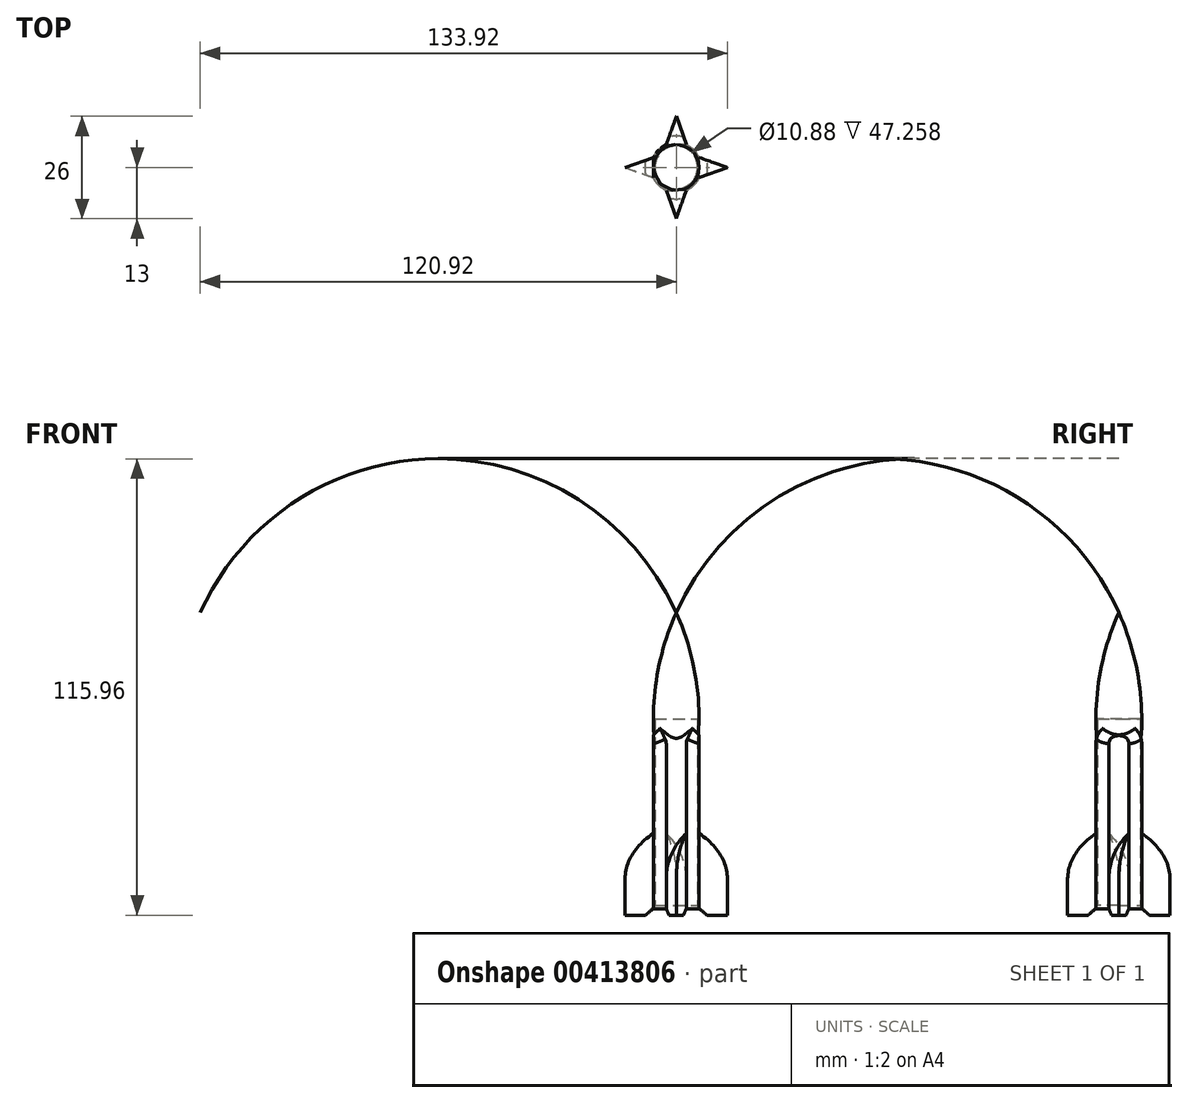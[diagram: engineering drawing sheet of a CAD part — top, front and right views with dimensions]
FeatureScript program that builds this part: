
annotation { "Feature Type Name" : "Feature", "Feature Type Description" : "" }
export const myFeature = defineFeature(function(context is Context, id is Id, definition is map)
    precondition{}
    {
        {
            var Q0;
            Q0=qCreatedBy(makeId("Top.planeOp"),FACE);
            var sketch = newSketch(context, id + "F0", { "sketchPlane" : qUnion([Q0])});
            skCircle(sketch, "E0", {"center": v(0, 0) * mm, "radius": 6.35 * mm});
            skLineSegment(sketch, "E1", {"start": v(5.82, 2.54) * mm, "end": v(13, 0) * mm});
            skLineSegment(sketch, "E2", {"start": v(13, 0) * mm, "end": v(5.82, -2.54) * mm});
            skLineSegment(sketch, "E3", {"start": v(-2.54, 5.82) * mm, "end": v(0, 13) * mm});
            skLineSegment(sketch, "E4", {"start": v(0, 13) * mm, "end": v(2.54, 5.82) * mm});
            skLineSegment(sketch, "E5", {"start": v(-5.82, 2.54) * mm, "end": v(-13, 0) * mm});
            skLineSegment(sketch, "E6", {"start": v(-13, 0) * mm, "end": v(-5.82, -2.54) * mm});
            skLineSegment(sketch, "E7", {"start": v(-2.54, -5.82) * mm, "end": v(0, -13) * mm});
            skLineSegment(sketch, "E8", {"start": v(0, -13) * mm, "end": v(2.54, -5.82) * mm});
            skCircle(sketch, "E9", {"center": v(0, 0) * mm, "radius": 5.44 * mm});
            skLineSegment(sketch, "E10", {"start": v(-5.82, -2.54) * mm, "end": v(-5.82, 2.54) * mm});
            skLineSegment(sketch, "E11", {"start": v(-2.54, -5.82) * mm, "end": v(2.54, -5.82) * mm});
            skLineSegment(sketch, "E12", {"start": v(5.82, -2.54) * mm, "end": v(5.82, 2.54) * mm});
            skLineSegment(sketch, "E13", {"start": v(2.54, 5.82) * mm, "end": v(-2.54, 5.82) * mm});
            skSolve(sketch);
        }
        {
            var Q0;
            {var subQ0=sQuery(id+"F0.wireOp",EDGE,"E0");var subQ5=makeQuery(id+"F0.imprint","INTERSECT",VERTEX,{"derivedFrom":[subQ0,sQuery(id+"F0.wireOp",EDGE,"E1")]});Q0=makeQuery(id+"F0.imprint","IMPRINT",FACE,{"disambiguationData":[TD([[makeQuery(id+"F0.imprint","IMPRINT",EDGE,{"disambiguationData":[TD([[subQ5,-1.0]])],"derivedFrom":subQ0}),1.0]])]});}
            var Q1;
            Q1=sQuery(id+"F0.wireOp",EDGE,"E0");
            extrude(context, id + "F1", {"entities" : qUnion([Q0]), "surfaceEntities" : qUnion([Q1]), "depth" : 50.8 * mm});
        }
        {
            var Q0;
            Q0 = qSketchRegion(id + "F0", true);
            extrude(context, id + "F2", {"entities" : qUnion([Q0]), "operationType" : NewBodyOperationType.ADD, "depth" : 25.4 * mm});
        }
        {
            var Q0;
            Q0=qCreatedBy(makeId("Front.planeOp"),FACE);
            var sketch = newSketch(context, id + "F3", { "sketchPlane" : qUnion([Q0])});
            skLineSegment(sketch, "E14", {"start": v(0, 49.8) * mm, "end": v(0, 76.85) * mm});
            skLineSegment(sketch, "E15", {"start": v(0, 49.8) * mm, "end": v(5.83, 49.8) * mm});
            skArc(sketch, "E16", {"start": v(5.83, 49.8) * mm, "mid": v(4.34, 63.63) * mm, "end": v(0, 76.85) * mm});
            skSolve(sketch);
        }
        {
            var Q0;
            Q0=makeQuery(id+"F2.opExtrude","CAP_EDGE",EDGE,{"disambiguationData":[OSD([sQuery(id+"F0.wireOp",EDGE,"E2")])],"isStart":false});
            var Q1;
            Q1=makeQuery(id+"F2.opExtrude","CAP_EDGE",EDGE,{"disambiguationData":[OSD([sQuery(id+"F0.wireOp",EDGE,"E4")])],"isStart":false});
            var Q2;
            Q2=makeQuery(id+"F2.opExtrude","CAP_EDGE",EDGE,{"disambiguationData":[OSD([sQuery(id+"F0.wireOp",EDGE,"E5")])],"isStart":false});
            var Q3;
            Q3=makeQuery(id+"F2.opExtrude","CAP_EDGE",EDGE,{"disambiguationData":[OSD([sQuery(id+"F0.wireOp",EDGE,"E7")])],"isStart":false});
            fillet(context, id + "F4", {"entities" : qUnion([Q0, Q1, Q2, Q3]), "radius" : 16.13 * mm, "tangentPropagation" : true, "allowEdgeOverflow" : false});
        }
        {
            var Q0;
            Q0=makeQuery(id+"F1.opExtrude","CAP_EDGE",EDGE,{"disambiguationData":[OSD([sQuery(id+"F0.wireOp",EDGE,"E9")])],"isStart":true});
            chamfer(context, id + "F5", {"entities" : qUnion([Q0]), "width" : 2.54 * mm, "tangentPropagation" : true});
        }
        {
            var Q0;
            Q0=makeQuery(id+"F3.imprint","IMPRINT",FACE,{"disambiguationData":[TD([[makeQuery(id+"F3.imprint","IMPRINT",EDGE,{"derivedFrom":sQuery(id+"F3.wireOp",EDGE,"E14")}),-1.0]])]});
            var Q1;
            Q1=sQuery(id+"F3.wireOp",EDGE,"E14");
            revolve(context, id + "F6", {"operationType" : NewBodyOperationType.ADD, "entities" : qUnion([Q0]), "axis" : qUnion([Q1]), "revolveType" : RevolveType.FULL});
        }
        {
            var Q0;
            Q0=makeQuery(id+"F1.opExtrude","CAP_EDGE",EDGE,{"disambiguationData":[OSD([sQuery(id+"F0.wireOp",EDGE,"E10")])],"isStart":false});
            var Q1;
            Q1=makeQuery(id+"F1.opExtrude","CAP_EDGE",EDGE,{"disambiguationData":[OSD([sQuery(id+"F0.wireOp",EDGE,"E12")])],"isStart":false});
            chamfer(context, id + "F7", {"entities" : qUnion([Q0, Q1]), "width" : 5.08 * mm, "tangentPropagation" : true});
        }
        {
            var Q0;
            Q0=makeQuery(id+"F1.opExtrude","CAP_EDGE",EDGE,{"disambiguationData":[OSD([sQuery(id+"F0.wireOp",EDGE,"E13")])],"isStart":false});
            var Q1;
            Q1=makeQuery(id+"F1.opExtrude","CAP_EDGE",EDGE,{"disambiguationData":[OSD([sQuery(id+"F0.wireOp",EDGE,"E11")])],"isStart":false});
            chamfer(context, id + "F8", {"entities" : qUnion([Q0, Q1]), "width" : 5.08 * mm, "tangentPropagation" : true});
        }
        {
            var Q0;
            {var subQ0=sQuery(id+"F0.wireOp",EDGE,"E12");var subQ1=sQuery(id+"F0.wireOp",EDGE,"E0");Q0=makeQuery(id+"F7.opChamfer","BLEND_EDGE",EDGE,{"blendedFrom":[makeQuery(id+"F1.opExtrude","CAP_EDGE",EDGE,{"disambiguationData":[OSD([subQ0])],"isStart":false}),makeQuery(id+"F1.opExtrude","SWEPT_FACE",FACE,{"disambiguationData":[OSD([subQ1]),TDD([makeQuery(id+"F0.imprint","IMPRINT",EDGE,{"disambiguationData":[TD([[makeQuery(id+"F0.imprint","INTERSECT",VERTEX,{"derivedFrom":[subQ1,sQuery(id+"F0.wireOp",EDGE,"E1"),subQ0]}),-1.0]])],"derivedFrom":subQ1})])]})],"blendedInto":[makeQuery(id+"F1.opExtrude","SWEPT_FACE",FACE,{"disambiguationData":[OSD([subQ1]),TDD([makeQuery(id+"F0.imprint","IMPRINT",EDGE,{"disambiguationData":[TD([[makeQuery(id+"F0.imprint","INTERSECT",VERTEX,{"derivedFrom":[subQ1,sQuery(id+"F0.wireOp",EDGE,"E1"),subQ0]}),-1.0]])],"derivedFrom":subQ1})])]})]});}
            var Q1;
            {var subQ0=sQuery(id+"F0.wireOp",EDGE,"E13");Q1=makeQuery(id+"F8.opChamfer","BLEND_EDGE",EDGE,{"blendedFrom":[makeQuery(id+"F1.opExtrude","CAP_EDGE",EDGE,{"disambiguationData":[OSD([subQ0])],"isStart":false}),makeQuery(id+"F1.opExtrude","SWEPT_FACE",FACE,{"disambiguationData":[OSD([subQ0])]})],"blendedInto":[makeQuery(id+"F1.opExtrude","SWEPT_FACE",FACE,{"disambiguationData":[OSD([subQ0])]})]});}
            var Q2;
            {var subQ0=sQuery(id+"F0.wireOp",EDGE,"E0");var subQ1=sQuery(id+"F0.wireOp",EDGE,"E10");Q2=makeQuery(id+"F7.opChamfer","BLEND_EDGE",EDGE,{"blendedFrom":[makeQuery(id+"F1.opExtrude","CAP_EDGE",EDGE,{"disambiguationData":[OSD([subQ1])],"isStart":false}),makeQuery(id+"F1.opExtrude","SWEPT_FACE",FACE,{"disambiguationData":[OSD([subQ0]),TDD([makeQuery(id+"F0.imprint","IMPRINT",EDGE,{"disambiguationData":[TD([[makeQuery(id+"F0.imprint","INTERSECT",VERTEX,{"derivedFrom":[subQ0,sQuery(id+"F0.wireOp",EDGE,"E3"),sQuery(id+"F0.wireOp",EDGE,"E13")]}),-1.0]])],"derivedFrom":subQ0})])]})],"blendedInto":[makeQuery(id+"F1.opExtrude","SWEPT_FACE",FACE,{"disambiguationData":[OSD([subQ0]),TDD([makeQuery(id+"F0.imprint","IMPRINT",EDGE,{"disambiguationData":[TD([[makeQuery(id+"F0.imprint","INTERSECT",VERTEX,{"derivedFrom":[subQ0,sQuery(id+"F0.wireOp",EDGE,"E3"),sQuery(id+"F0.wireOp",EDGE,"E13")]}),-1.0]])],"derivedFrom":subQ0})])]})]});}
            var Q3;
            {var subQ0=sQuery(id+"F0.wireOp",EDGE,"E11");Q3=makeQuery(id+"F8.opChamfer","BLEND_EDGE",EDGE,{"blendedFrom":[makeQuery(id+"F1.opExtrude","CAP_EDGE",EDGE,{"disambiguationData":[OSD([subQ0])],"isStart":false}),makeQuery(id+"F1.opExtrude","SWEPT_FACE",FACE,{"disambiguationData":[OSD([subQ0])]})],"blendedInto":[makeQuery(id+"F1.opExtrude","SWEPT_FACE",FACE,{"disambiguationData":[OSD([subQ0])]})]});}
            fillet(context, id + "F9", {"entities" : qUnion([Q0, Q1, Q2, Q3]), "radius" : 5.08 * mm, "tangentPropagation" : true, "allowEdgeOverflow" : false});
        }
    });
